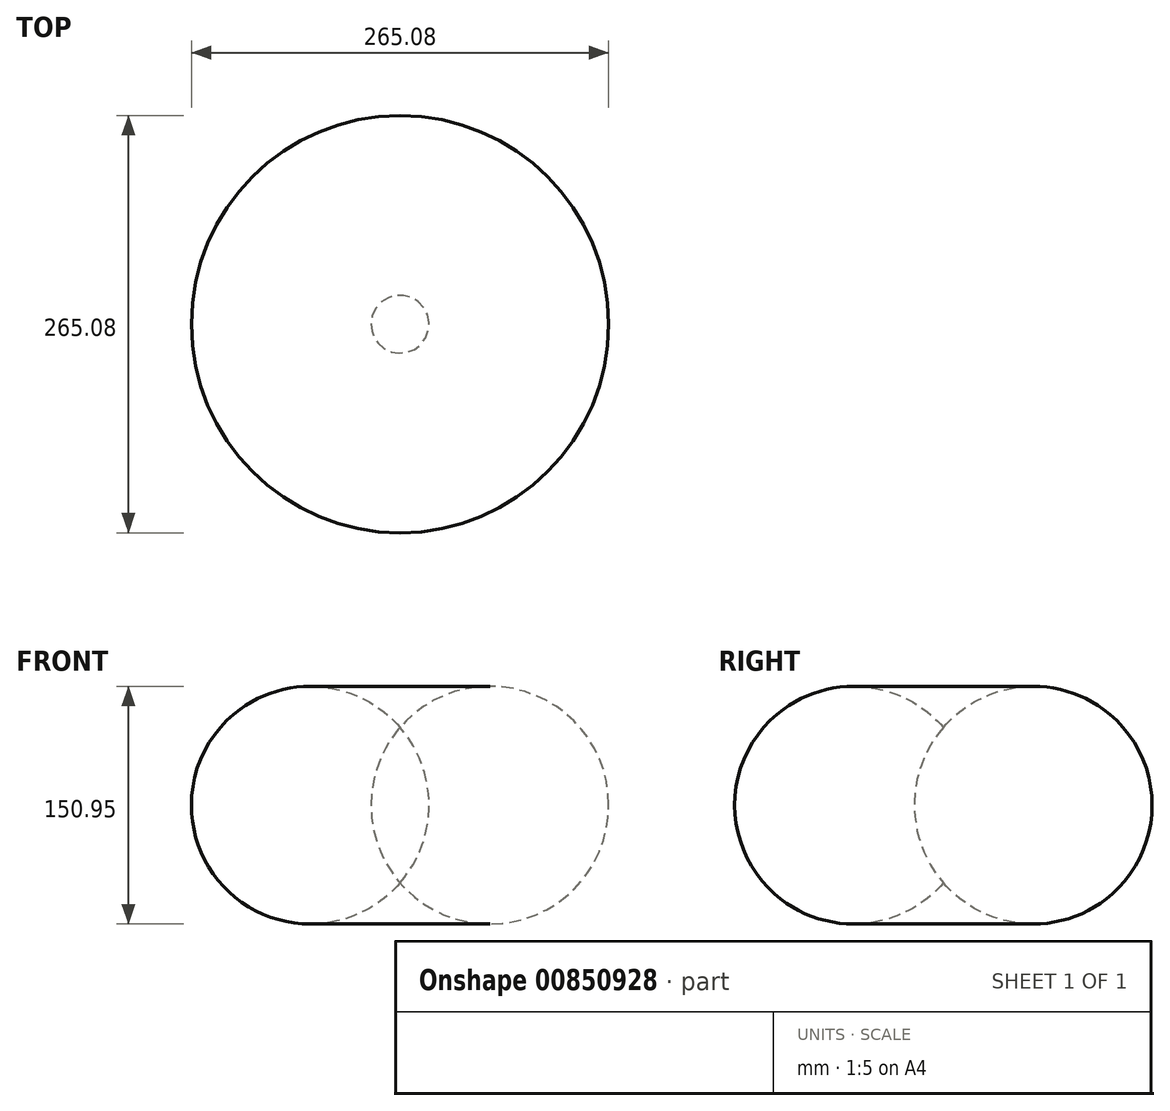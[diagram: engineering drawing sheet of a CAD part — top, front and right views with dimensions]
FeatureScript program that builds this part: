
annotation { "Feature Type Name" : "Feature", "Feature Type Description" : "" }
export const myFeature = defineFeature(function(context is Context, id is Id, definition is map)
    precondition{}
    {
        {
            var Q0;
            Q0=qCreatedBy(makeId("Front.planeOp"),FACE);
            var sketch = newSketch(context, id + "F0", { "sketchPlane" : qUnion([Q0])});
            skLineSegment(sketch, "E0", {"start": v(-38.92, 70.94) * mm, "end": v(-38.92, -27.87) * mm});
            skArc(sketch, "E1", {"start": v(-38.92, -27.87) * mm, "mid": v(-20.5, 21.54) * mm, "end": v(-38.92, 70.94) * mm});
            skSolve(sketch);
        }
        {
            var Q0;
            Q0=makeQuery(id+"F0.imprint","IMPRINT",FACE,{"disambiguationData":[TD([[makeQuery(id+"F0.imprint","IMPRINT",EDGE,{"derivedFrom":sQuery(id+"F0.wireOp",EDGE,"E0")}),1.0]])]});
            var Q1;
            Q1=sQuery(id+"F0.wireOp",EDGE,"E0");
            revolve(context, id + "F1", {"surfaceOperationType" : NewSurfaceOperationType.NEW, "entities" : qUnion([Q0]), "axis" : qUnion([Q1]), "revolveType" : RevolveType.FULL});
        }
    });
